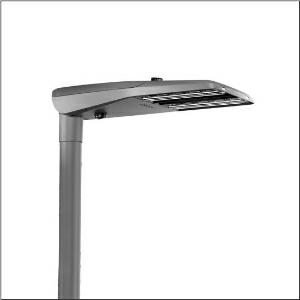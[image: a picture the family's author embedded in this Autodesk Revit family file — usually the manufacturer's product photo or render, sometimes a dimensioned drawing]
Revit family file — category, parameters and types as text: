
# Revit family: streetlight_sl_11_iq_midi___st1_2a_5xc3a11y08me_f942
name_source: partatom
category: Lighting Fixtures
units: mm (PartAtom-declared; Revit-internal decimal feet)

## family parameters
Cut with Voids When Loaded = No
Host = Face
Light Source = No
Part Type = Normal
Room Calculation Point = No
Round Connector Dimension = Use Diameter
Shared = No

## types (1)
- --- (1 x LED, 11200 lm, 123.4 W, 1800K)
    Apparent Load = 123 VA
    CIE Flux Codes = 32 70 96 100 100
    Color Rendering = 70
    Color Temperature = 1800K
    Default Elevation = 1800 mm  [stored 5.90551 ft]
    Description = Streetlight SL 11 iQ midi, mast luminaire, primary light control with 3 zone facetted reflector, of plastic, silver coated, highly specular, primary optical cover: cover, of PMMA, transparent, light distribution: ST1.2a, light emission: direct distribution, primary light characteristic: asymmetric, installation type: post-top, side-entry, lamps: LED, High Power LED, rated values: 11.200lm | 123,4W | 90,8lm/W (begin service life); end service life: 11.200lm | 130,9W; at 50% lumin. flux: 5.600lm | 54,1W | 103,5lm/W, colour temperature: 1800K, colour rendering: CRI > 70, light colour: 718, light setting 1 begin service life: 100% | 11.200lm | 123,4W | 90,8lm/W | 1.800K, light setting 1 end service life: 130,9W, further light settings possible, control: pre-setting: logarithmic dimming characteristic, Street-Remote, Auto-Match, Temp-Guard, Lumen-Switch, Night-Set, Smart-Wire, Light-Fading, Desk-Remote (wireless, voltage-free reading and setting of iQ features in the workshop via application-optimized NFC function/RFID function), optimised constant luminous flux control (CLO 2.0), with cable H07RN-F 5x 1.5mm², mains connection: 230..240V, AC, 50/60Hz, connection cable pre-assembled, cable length: 12,5m, luminaire housing, of diecast aluminium, powder-coated, Siteco® metallic grey (DB 702S), please order mast flange separately, inclination adjustable without tools: 0°, 5°, 10°, 15° (post-top) | 0°, -5°, -10°, -15° (side-entry), sealing non-destructively replaceable, multi-level sealing system, length: 780mm, width: 376mm, height: 118mm, mast flange for spigot size: 42mm (side-entry): 5XC10008XM4, 60/48mm (side-entry/post-top): 5XC10108XM2, 76/60mm (side-entry/post-top): 5XC10108XM1, equipment: Power, Smart Interface below and above, protection rating (complete): IP66, insulation class (complete): insulation class II (safety insulation), certification: CE, ENEC, ENEC+, VDE, UKCA, impact resistance: IK10, permissible operating ambient temperature for outdoor applications: -25..+50°C, standard-compliant lighting for roads and squares, Environmental Product Declaration (EPD) tested and certified by an independent institute, packaging unit: 1 piece

Light Distribution: ST1.2a
    Height = 118 mm
    Lamp = 1 x LED
    Lamp Light Flux = 11200 lm
    Lamp Power = 123.4 W
    Lamp count = 1
    Length = 780 mm
    Luminous efficacy = 91 lm/W
    Manufacturer = Siteco
    ModVariant = No
    Model = 5XC3A11Y08ME
    Number of Poles = 1
    OnlyDefault = Yes
    Power Factor = 1
    Product Name = Streetlight SL 11 iQ midi | ST1.2a
    Product group = mast luminaire | pylon top
    ProductGroupID = 6100
    Protection Class = Protection class II
    Protection Degree = IP 66
    RLX_Detail_Level = 1
    RLX_Emergency_Light_Flux = 0 lm
    RLX_Emergency_Type = 0
    RLX_Emergency_Type_DB = No
    RlxData = <blob elided: 69825 chars, md5=4fa06193>
    Socket = socket
    Standby Power = 0 W
    System Light Flux = 11200 lm
    System Power = 123 W
    Type Comments = factory setting: luminous flux: 100 % | dim-lin: 254 | 553 mA
    Type Image = l_1004429.jpg
    URL = http://relux.com
    VarID = @adj_060685
    Voltage = 0 V
    Weight = 0.00 kg
    Width = 376 mm

note: [stored X ft] marks values corroborated as IEEE doubles in the binary element streams (Revit-internal decimal feet)

## geometry (parser evidence)
native form markers: Blend x4, Sweep x10
no freeform markers — native parametric forms only
